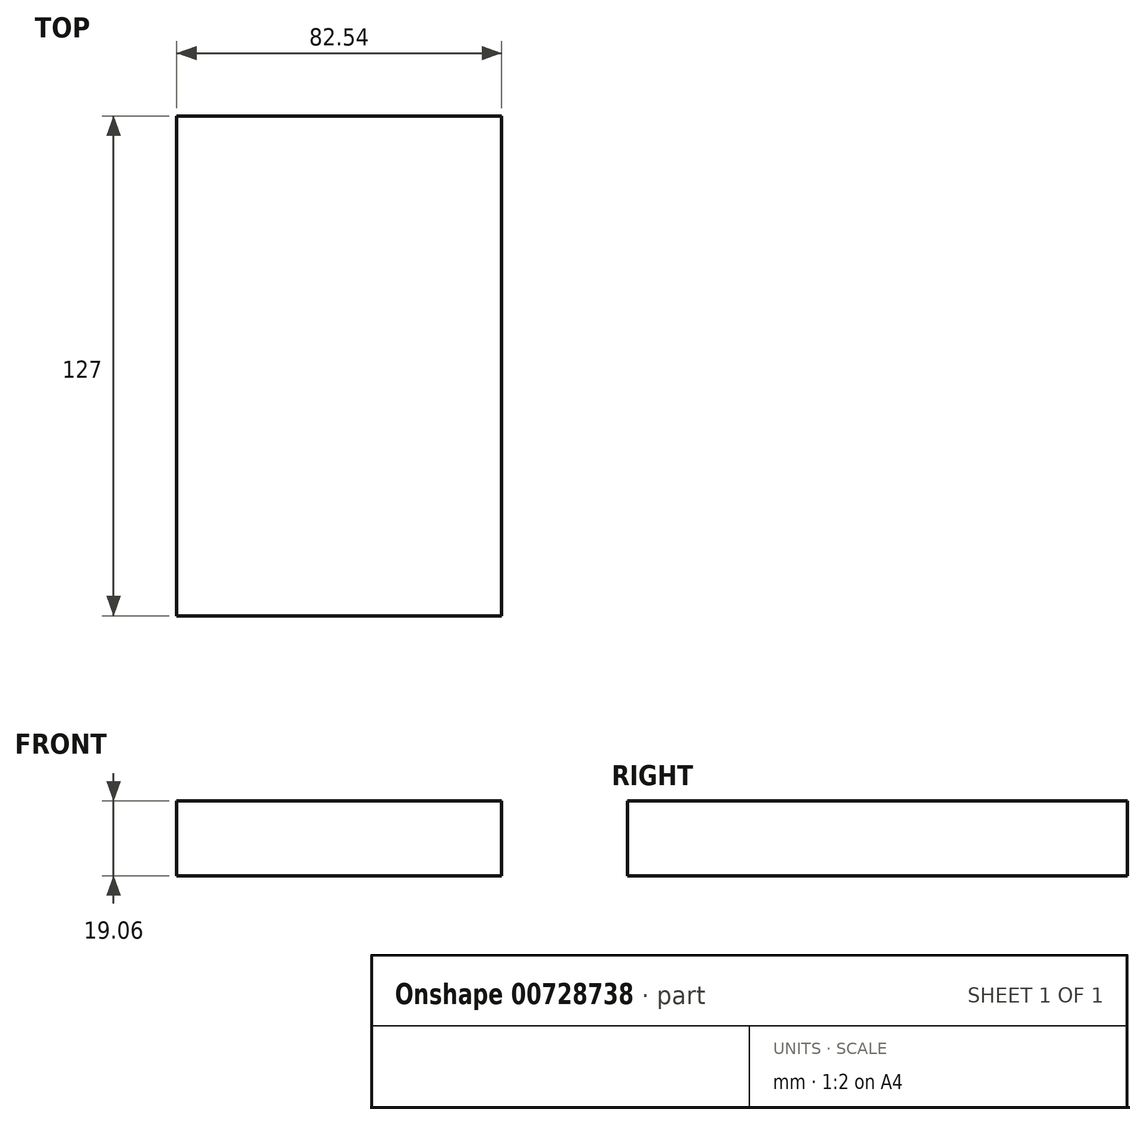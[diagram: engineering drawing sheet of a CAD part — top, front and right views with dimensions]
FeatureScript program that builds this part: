
annotation { "Feature Type Name" : "Feature", "Feature Type Description" : "" }
export const myFeature = defineFeature(function(context is Context, id is Id, definition is map)
    precondition{}
    {
        {
            var Q0;
            Q0=qCreatedBy(makeId("Front.planeOp"),FACE);
            var sketch = newSketch(context, id + "F0", { "sketchPlane" : qUnion([Q0])});
            skLineSegment(sketch, "E0.bottom", {"start": v(-41.27, -9.53) * mm, "end": v(41.28, -9.53) * mm});
            skLineSegment(sketch, "E0.top", {"start": v(-41.28, 9.53) * mm, "end": v(41.28, 9.53) * mm});
            skLineSegment(sketch, "E0.left", {"start": v(-41.28, -9.53) * mm, "end": v(-41.28, 9.53) * mm});
            skLineSegment(sketch, "E0.right", {"start": v(41.28, -9.53) * mm, "end": v(41.28, 9.53) * mm});
            skPoint(sketch, "E0.middle", {"position": v(0, 0) * mm});
            skLineSegment(sketch, "E1.bottom", {"start": v(62.39, 38.1) * mm, "end": v(113.19, 38.1) * mm});
            skLineSegment(sketch, "E1.top", {"start": v(62.39, 66.67) * mm, "end": v(113.19, 66.67) * mm});
            skLineSegment(sketch, "E1.left", {"start": v(62.39, 38.1) * mm, "end": v(62.39, 66.67) * mm});
            skLineSegment(sketch, "E1.right", {"start": v(113.19, 38.1) * mm, "end": v(113.19, 66.67) * mm});
            skPoint(sketch, "E1.middle", {"position": v(87.79, 52.39) * mm});
            skLineSegment(sketch, "E2", {"start": v(41.28, 9.52) * mm, "end": v(41.28, 34.43) * mm});
            skArc(sketch, "E3", {"start": v(41.27, 34.43) * mm, "mid": v(52.76, 49.69) * mm, "end": v(70.6, 42.88) * mm});
            skLineSegment(sketch, "E4", {"start": v(70.6, 42.88) * mm, "end": v(85.72, 42.88) * mm});
            skSolve(sketch);
        }
        {
            var Q0;
            Q0=makeQuery(id+"F0.imprint","IMPRINT",FACE,{"disambiguationData":[TD([[makeQuery(id+"F0.imprint","IMPRINT",EDGE,{"derivedFrom":sQuery(id+"F0.wireOp",EDGE,"E0.bottom")}),1.0]])]});
            extrude(context, id + "F1", {"entities" : qUnion([Q0]), "depth" : 127 * mm, "offsetDistance" : 25.4 * mm});
        }
    });
